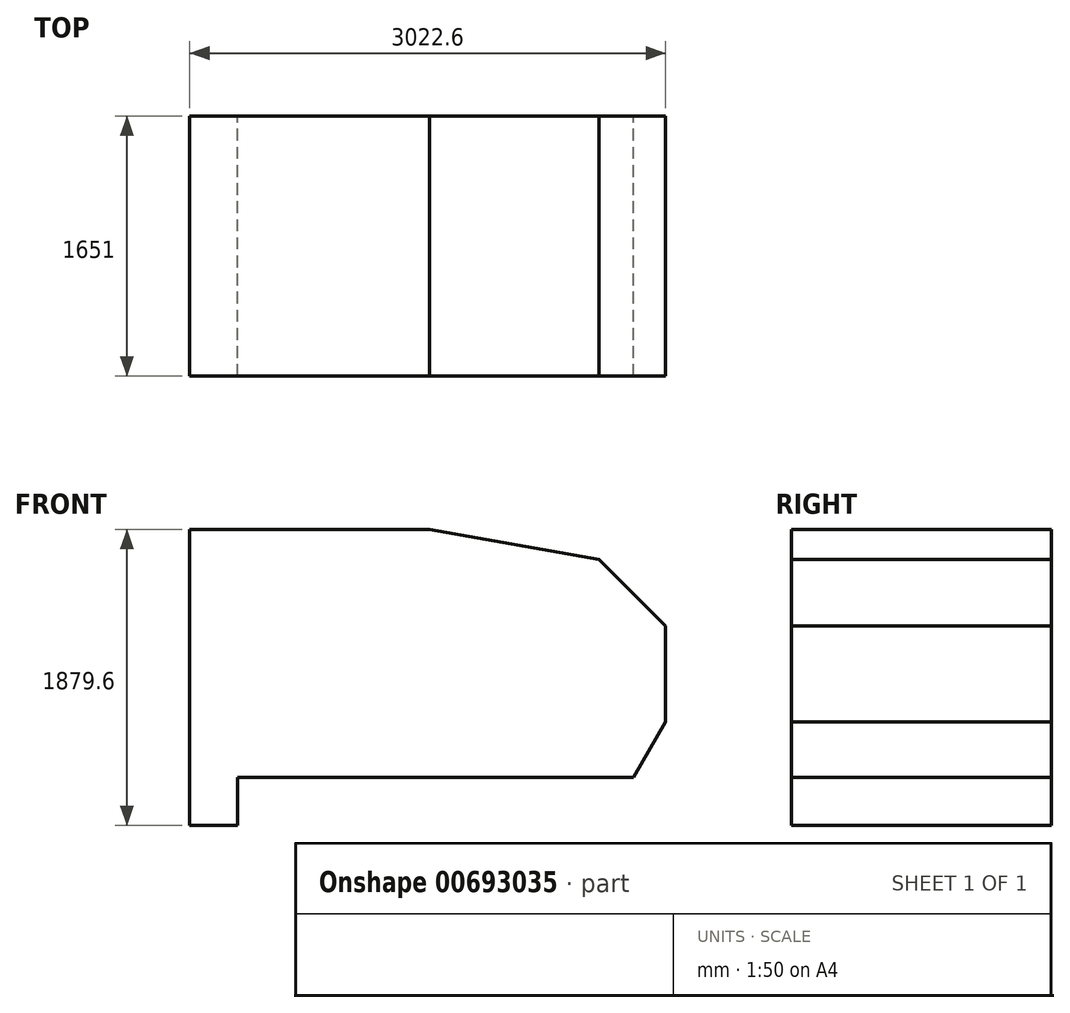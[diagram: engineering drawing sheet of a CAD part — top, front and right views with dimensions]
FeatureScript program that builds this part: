
annotation { "Feature Type Name" : "Feature", "Feature Type Description" : "" }
export const myFeature = defineFeature(function(context is Context, id is Id, definition is map)
    precondition{}
    {
        {
            var Q0;
            Q0=qCreatedBy(makeId("Front.planeOp"),FACE);
            var sketch = newSketch(context, id + "F0", { "sketchPlane" : qUnion([Q0])});
            skLineSegment(sketch, "E0.bottom", {"start": v(1219.2, -152.4) * mm, "end": v(-1219.2, -152.4) * mm});
            skLineSegment(sketch, "E0.top", {"start": v(1219.2, 152.4) * mm, "end": v(-1219.2, 152.4) * mm});
            skLineSegment(sketch, "E0.left", {"start": v(1219.2, -152.4) * mm, "end": v(1219.2, 152.4) * mm});
            skLineSegment(sketch, "E0.right", {"start": v(-1219.2, -152.4) * mm, "end": v(-1219.2, 152.4) * mm});
            skPoint(sketch, "E0.middle", {"position": v(0, 0) * mm});
            skLineSegment(sketch, "E1", {"start": v(1219.2, 152.4) * mm, "end": v(1295.4, 152.4) * mm});
            skLineSegment(sketch, "E2", {"start": v(1295.4, 152.4) * mm, "end": v(1498.6, 504.35) * mm});
            skLineSegment(sketch, "E3", {"start": v(1498.6, 504.35) * mm, "end": v(1498.6, 1113.95) * mm});
            skLineSegment(sketch, "E4", {"start": v(1498.6, 1113.95) * mm, "end": v(1074.88, 1537.67) * mm});
            skLineSegment(sketch, "E5", {"start": v(1074.88, 1537.67) * mm, "end": v(0, 1727.2) * mm});
            skLineSegment(sketch, "E6", {"start": v(0, 1727.2) * mm, "end": v(-1524, 1727.2) * mm});
            skLineSegment(sketch, "E7", {"start": v(-1524, 1727.2) * mm, "end": v(-1524, -152.4) * mm});
            skLineSegment(sketch, "E8", {"start": v(-1524, -152.4) * mm, "end": v(-1219.2, -152.4) * mm});
            skSolve(sketch);
        }
        {
            var Q0;
            Q0=makeQuery(id+"F0.imprint","IMPRINT",FACE,{"disambiguationData":[TD([[makeQuery(id+"F0.imprint","IMPRINT",EDGE,{"derivedFrom":sQuery(id+"F0.wireOp",EDGE,"E0.top")}),-1.0]])]});
            extrude(context, id + "F1", {"entities" : qUnion([Q0]), "depth" : 1651 * mm, "offsetDistance" : 25.4 * mm});
        }
    });
